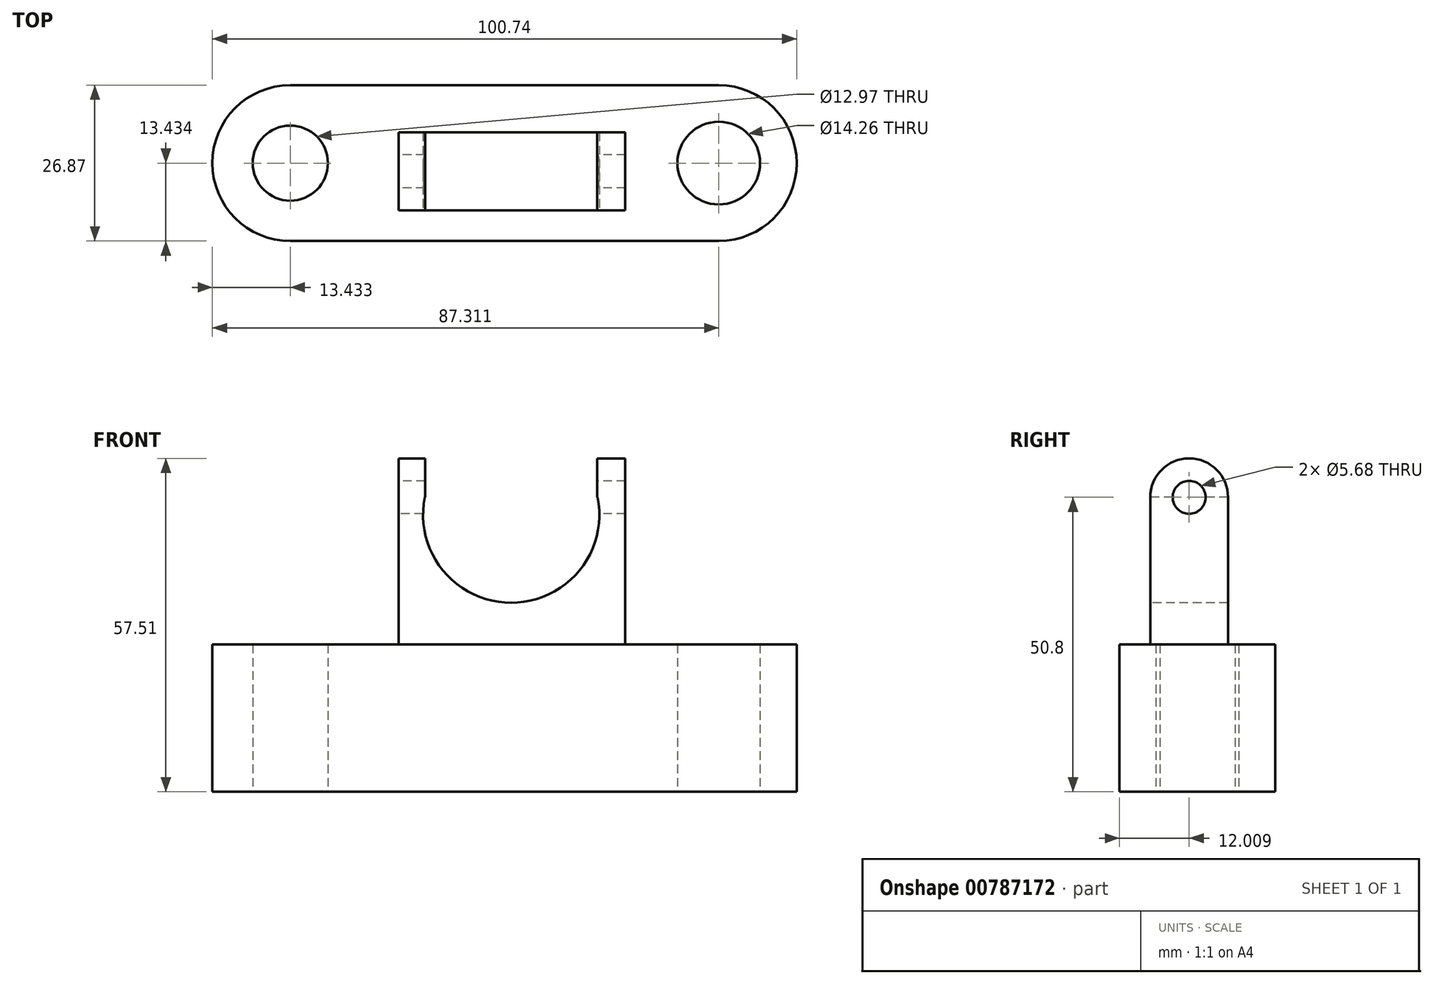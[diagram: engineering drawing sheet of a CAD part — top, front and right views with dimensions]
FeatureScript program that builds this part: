
annotation { "Feature Type Name" : "Feature", "Feature Type Description" : "" }
export const myFeature = defineFeature(function(context is Context, id is Id, definition is map)
    precondition{}
    {
        {
            var Q0;
            Q0=qCreatedBy(makeId("Top.planeOp"),FACE);
            var sketch = newSketch(context, id + "F0", { "sketchPlane" : qUnion([Q0])});
            skLineSegment(sketch, "E0.bottom", {"start": v(-36.65, 17.67) * mm, "end": v(37.23, 17.67) * mm});
            skLineSegment(sketch, "E0.top", {"start": v(-36.65, -9.2) * mm, "end": v(37.23, -9.2) * mm});
            skLineSegment(sketch, "E0.left", {"start": v(-36.65, 17.67) * mm, "end": v(-36.65, -9.2) * mm});
            skLineSegment(sketch, "E0.right", {"start": v(37.23, 17.67) * mm, "end": v(37.23, -9.2) * mm});
            skArc(sketch, "E1", {"start": v(-36.65, 17.67) * mm, "mid": v(-50.08, 4.23) * mm, "end": v(-36.65, -9.2) * mm});
            skArc(sketch, "E2", {"start": v(37.23, -9.2) * mm, "mid": v(50.66, 4.23) * mm, "end": v(37.23, 17.67) * mm});
            skCircle(sketch, "E3", {"center": v(-36.65, 4.23) * mm, "radius": 6.48 * mm});
            skCircle(sketch, "E4", {"center": v(37.23, 4.23) * mm, "radius": 7.13 * mm});
            skLineSegment(sketch, "E5.bottom", {"start": v(-17.99, 9.52) * mm, "end": v(21.12, 9.52) * mm});
            skLineSegment(sketch, "E5.left", {"start": v(-17.99, 9.52) * mm, "end": v(-17.99, 0) * mm});
            skLineSegment(sketch, "E5.right", {"start": v(21.12, 9.52) * mm, "end": v(21.12, 0) * mm});
            skLineSegment(sketch, "E6.top", {"start": v(-17.99, -3.9) * mm, "end": v(21.12, -3.9) * mm});
            skLineSegment(sketch, "E6.left", {"start": v(-17.99, 0) * mm, "end": v(-17.99, -3.9) * mm});
            skLineSegment(sketch, "E6.right", {"start": v(21.12, 0) * mm, "end": v(21.12, -3.9) * mm});
            skSolve(sketch);
        }
        {
            var Q0;
            {var subQ0=sQuery(id+"F0.wireOp",EDGE,"E1");Q0=makeQuery(id+"F0.imprint","IMPRINT",FACE,{"disambiguationData":[TD([[makeQuery(id+"F0.imprint","IMPRINT",EDGE,{"derivedFrom":subQ0}),1.0]])]});}
            var Q1;
            {var subQ5=sQuery(id+"F0.wireOp",EDGE,"E0.bottom");Q1=makeQuery(id+"F0.imprint","IMPRINT",FACE,{"disambiguationData":[TD([[makeQuery(id+"F0.imprint","IMPRINT",EDGE,{"derivedFrom":subQ5}),-1.0]])]});}
            var Q2;
            {var subQ0=sQuery(id+"F0.wireOp",EDGE,"E2");Q2=makeQuery(id+"F0.imprint","IMPRINT",FACE,{"disambiguationData":[TD([[makeQuery(id+"F0.imprint","IMPRINT",EDGE,{"derivedFrom":subQ0}),1.0]])]});}
            extrude(context, id + "F1", {"entities" : qUnion([Q0, Q1, Q2]), "depth" : 25.4 * mm, "offsetDistance" : 25.4 * mm});
        }
        {
            var Q0;
            Q0=makeQuery(id+"F0.imprint","IMPRINT",FACE,{"disambiguationData":[TD([[makeQuery(id+"F0.imprint","IMPRINT",EDGE,{"derivedFrom":sQuery(id+"F0.wireOp",EDGE,"E5.bottom")}),-1.0]])]});
            extrude(context, id + "F2", {"entities" : qUnion([Q0]), "operationType" : NewBodyOperationType.ADD, "depth" : 50.8 * mm, "offsetDistance" : 25.4 * mm});
        }
        {
            var Q0;
            Q0=makeQuery(id+"F2.opExtrude","SWEPT_FACE",FACE,{"disambiguationData":[OSD([sQuery(id+"F0.wireOp",EDGE,"E5.left"),sQuery(id+"F0.wireOp",EDGE,"E6.left")])]});
            var sketch = newSketch(context, id + "F3", { "sketchPlane" : qUnion([Q0])});
            skArc(sketch, "E7", {"start": v(3.9, 50.8) * mm, "mid": v(-2.8, 57.51) * mm, "end": v(-9.52, 50.8) * mm});
            skSolve(sketch);
        }
        {
            var Q0;
            Q0=makeQuery(id+"F2.opExtrude","SWEPT_FACE",FACE,{"disambiguationData":[OSD([sQuery(id+"F0.wireOp",EDGE,"E6.top")])]});
            var sketch = newSketch(context, id + "F4", { "sketchPlane" : qUnion([Q0])});
            skArc(sketch, "E8", {"start": v(-13.45, 50.8) * mm, "mid": v(1.44, 32.6) * mm, "end": v(16.34, 50.8) * mm});
            skSolve(sketch);
        }
        {
            var Q0;
            {var subQ0=sQuery(id+"F4.wireOp",EDGE,"E8");Q0=makeQuery(id+"F4.imprint","IMPRINT",FACE,{"disambiguationData":[TD([[makeQuery(id+"F4.imprint","IMPRINT",EDGE,{"derivedFrom":subQ0}),1.0]])]});}
            extrude(context, id + "F5", {"entities" : qUnion([Q0]), "operationType" : NewBodyOperationType.REMOVE, "oppositeDirection" : true, "depth" : 25.4 * mm, "offsetDistance" : 25.4 * mm});
        }
        {
            var Q0;
            Q0=makeQuery(id+"F3.imprint","IMPRINT",FACE,{"disambiguationData":[TD([[makeQuery(id+"F3.imprint","IMPRINT",EDGE,{"derivedFrom":sQuery(id+"F3.wireOp",EDGE,"E7")}),1.0]])]});
            extrude(context, id + "F6", {"entities" : qUnion([Q0]), "operationType" : NewBodyOperationType.ADD, "oppositeDirection" : true, "depth" : 4.57 * mm, "offsetDistance" : 25.4 * mm});
        }
        {
            var Q0;
            Q0=makeQuery(id+"F2.opExtrude","SWEPT_FACE",FACE,{"disambiguationData":[OSD([sQuery(id+"F0.wireOp",EDGE,"E5.right"),sQuery(id+"F0.wireOp",EDGE,"E6.right")])]});
            var sketch = newSketch(context, id + "F7", { "sketchPlane" : qUnion([Q0])});
            skArc(sketch, "E9", {"start": v(9.52, 50.8) * mm, "mid": v(2.8, 57.51) * mm, "end": v(-3.9, 50.8) * mm});
            skSolve(sketch);
        }
        {
            var Q0;
            Q0=makeQuery(id+"F7.imprint","IMPRINT",FACE,{"disambiguationData":[TD([[makeQuery(id+"F7.imprint","IMPRINT",EDGE,{"derivedFrom":sQuery(id+"F7.wireOp",EDGE,"E9")}),1.0]])]});
            extrude(context, id + "F8", {"entities" : qUnion([Q0]), "operationType" : NewBodyOperationType.ADD, "oppositeDirection" : true, "depth" : 4.83 * mm, "offsetDistance" : 25.4 * mm});
        }
        {
            var Q0;
            {var subQ0=sQuery(id+"F0.wireOp",EDGE,"E6.left");var subQ1=sQuery(id+"F0.wireOp",EDGE,"E5.left");Q0=makeQuery(id+"F6.boolean.opBoolean","MERGE",FACE,{"derivedFrom":[makeQuery(id+"F2.opExtrude","SWEPT_FACE",FACE,{"disambiguationData":[OSD([subQ1,subQ0])]}),makeQuery(id+"F6.opExtrude","CAP_FACE",FACE,{"disambiguationData":[OSD([subQ1,subQ0,sQuery(id+"F3.wireOp",EDGE,"E7")])],"isStart":true})]});}
            var sketch = newSketch(context, id + "F9", { "sketchPlane" : qUnion([Q0])});
            skCircle(sketch, "E10", {"center": v(-2.8, 50.8) * mm, "radius": 2.84 * mm});
            skSolve(sketch);
        }
        {
            var Q0;
            Q0=makeQuery(id+"F9.imprint","IMPRINT",FACE,{"disambiguationData":[TD([[makeQuery(id+"F9.imprint","IMPRINT",EDGE,{"derivedFrom":sQuery(id+"F9.wireOp",EDGE,"E10")}),1.0]])]});
            extrude(context, id + "F10", {"entities" : qUnion([Q0]), "operationType" : NewBodyOperationType.REMOVE, "oppositeDirection" : true, "depth" : 49.78 * mm, "offsetDistance" : 25.4 * mm});
        }
    });
